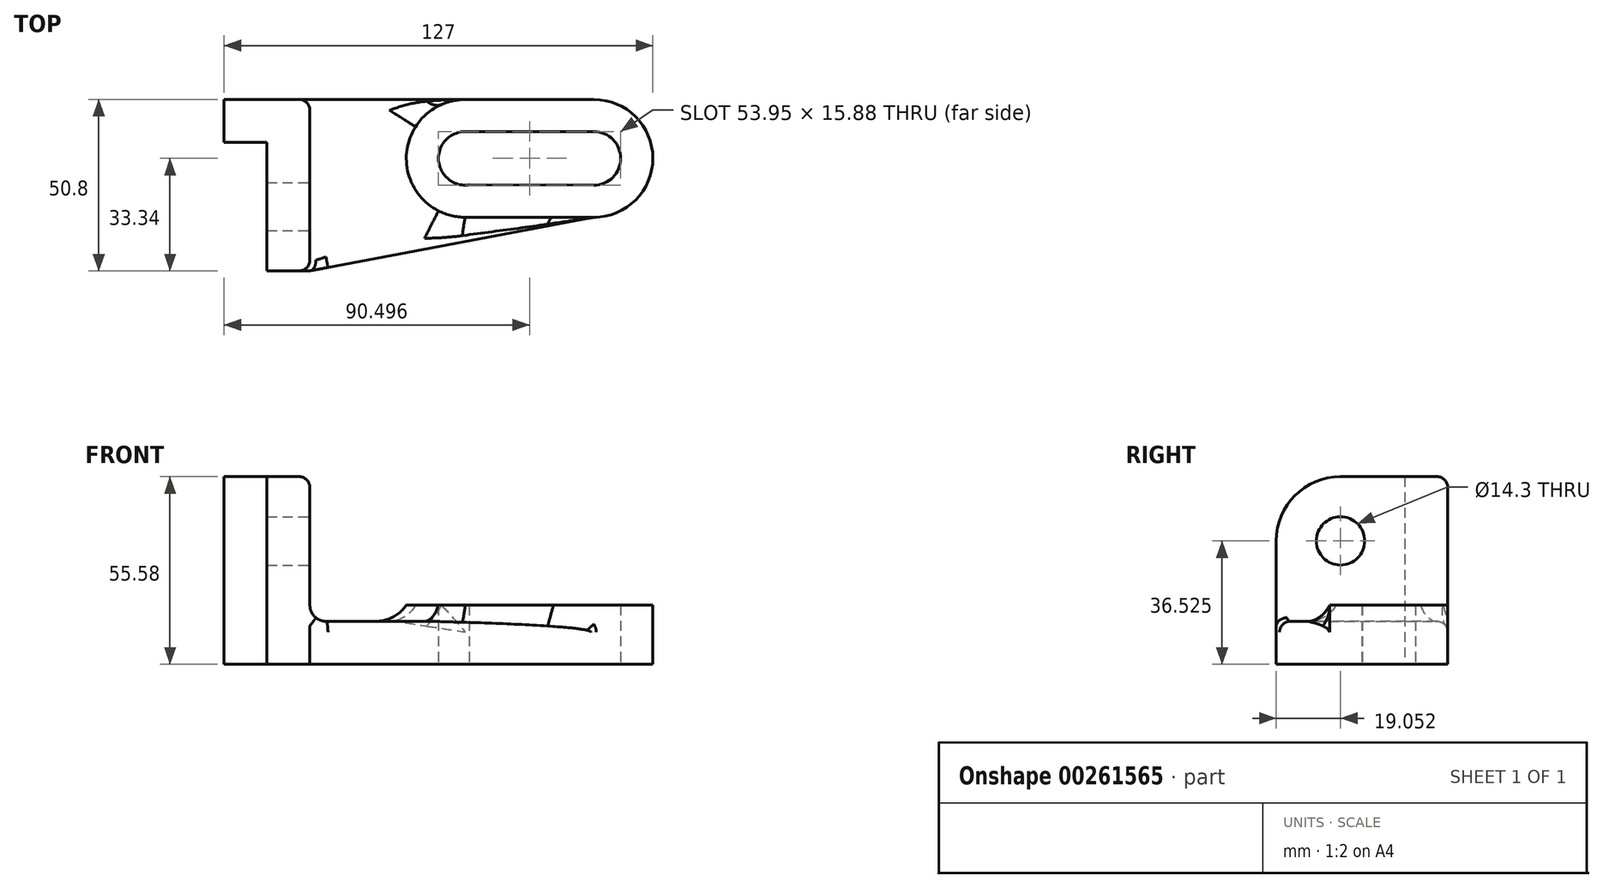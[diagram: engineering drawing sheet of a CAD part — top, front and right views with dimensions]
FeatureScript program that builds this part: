
annotation { "Feature Type Name" : "Feature", "Feature Type Description" : "" }
export const myFeature = defineFeature(function(context is Context, id is Id, definition is map)
    precondition{}
    {
        {
            var Q0;
            Q0=qCreatedBy(makeId("Top.planeOp"),FACE);
            var sketch = newSketch(context, id + "F0", { "sketchPlane" : qUnion([Q0])});
            skArc(sketch, "E0", {"start": v(-25.36, 8.79) * mm, "mid": v(-7.9, 26.25) * mm, "end": v(-25.36, 43.71) * mm});
            skArc(sketch, "E1", {"start": v(-25.36, 18.31) * mm, "mid": v(-17.43, 26.25) * mm, "end": v(-25.36, 34.19) * mm});
            skLineSegment(sketch, "E2", {"start": v(-25.36, 43.71) * mm, "end": v(-63.45, 43.71) * mm});
            skLineSegment(sketch, "E3", {"start": v(-25.36, 8.79) * mm, "end": v(-63.46, 8.79) * mm});
            skArc(sketch, "E4", {"start": v(-63.45, 43.71) * mm, "mid": v(-80.93, 26.26) * mm, "end": v(-63.46, 8.79) * mm});
            skArc(sketch, "E5", {"start": v(-63.46, 34.19) * mm, "mid": v(-71.38, 25.67) * mm, "end": v(-62.3, 18.4) * mm});
            skLineSegment(sketch, "E6", {"start": v(-63.46, 34.19) * mm, "end": v(-25.36, 34.19) * mm});
            skLineSegment(sketch, "E7", {"start": v(-64.66, 18.4) * mm, "end": v(-25.36, 18.31) * mm});
            skLineSegment(sketch, "E8", {"start": v(-63.45, 43.71) * mm, "end": v(-109.5, 43.71) * mm});
            skLineSegment(sketch, "E9", {"start": v(-109.5, 43.71) * mm, "end": v(-109.5, -7.09) * mm});
            skLineSegment(sketch, "E10", {"start": v(-109.5, -7.09) * mm, "end": v(-25.36, 8.79) * mm});
            skLineSegment(sketch, "E11", {"start": v(-109.5, 43.71) * mm, "end": v(-122.2, 43.71) * mm});
            skLineSegment(sketch, "E12", {"start": v(-122.2, 31.01) * mm, "end": v(-122.2, -7.09) * mm});
            skLineSegment(sketch, "E13", {"start": v(-122.2, -7.09) * mm, "end": v(-109.5, -7.09) * mm});
            skLineSegment(sketch, "E14", {"start": v(-122.2, 31.01) * mm, "end": v(-134.9, 31.01) * mm});
            skLineSegment(sketch, "E15", {"start": v(-134.9, 31.01) * mm, "end": v(-134.9, 43.71) * mm});
            skLineSegment(sketch, "E16", {"start": v(-134.9, 43.71) * mm, "end": v(-122.2, 43.71) * mm});
            skSolve(sketch);
        }
        {
            var Q0;
            Q0 = qSketchRegion(id + "F0", true);
            extrude(context, id + "F1", {"entities" : qUnion([Q0]), "depth" : 12.7 * mm});
        }
        {
            var Q0;
            Q0=makeQuery(id+"F0.imprint","IMPRINT",FACE,{"disambiguationData":[TD([[makeQuery(id+"F0.imprint","IMPRINT",EDGE,{"derivedFrom":sQuery(id+"F0.wireOp",EDGE,"E0")}),1.0]])]});
            extrude(context, id + "F2", {"entities" : qUnion([Q0]), "operationType" : NewBodyOperationType.ADD, "depth" : 17.48 * mm});
        }
        {
            var Q0;
            Q0=makeQuery(id+"F0.imprint","IMPRINT",FACE,{"disambiguationData":[TD([[makeQuery(id+"F0.imprint","IMPRINT",EDGE,{"derivedFrom":sQuery(id+"F0.wireOp",EDGE,"E9")}),-1.0]])]});
            extrude(context, id + "F3", {"entities" : qUnion([Q0]), "operationType" : NewBodyOperationType.ADD, "depth" : 55.58 * mm});
        }
        {
            var Q0;
            Q0=makeQuery(id+"F3.boolean.opBoolean","INTERSECT",EDGE,{"derivedFrom":[makeQuery(id+"F1.opExtrude","CAP_FACE",FACE,{"disambiguationData":[OSD([sQuery(id+"F0.wireOp",EDGE,"E0"),sQuery(id+"F0.wireOp",EDGE,"E1"),sQuery(id+"F0.wireOp",EDGE,"E2"),sQuery(id+"F0.wireOp",EDGE,"E5"),sQuery(id+"F0.wireOp",EDGE,"E6"),sQuery(id+"F0.wireOp",EDGE,"E7"),sQuery(id+"F0.wireOp",EDGE,"E8"),sQuery(id+"F0.wireOp",EDGE,"E10"),sQuery(id+"F0.wireOp",EDGE,"E11"),sQuery(id+"F0.wireOp",EDGE,"E12"),sQuery(id+"F0.wireOp",EDGE,"E13"),sQuery(id+"F0.wireOp",EDGE,"E14"),sQuery(id+"F0.wireOp",EDGE,"E15"),sQuery(id+"F0.wireOp",EDGE,"E16")])],"isStart":false}),makeQuery(id+"F3.opExtrude","SWEPT_FACE",FACE,{"disambiguationData":[OSD([sQuery(id+"F0.wireOp",EDGE,"E9")])]})]});
            fillet(context, id + "F4", {"entities" : qUnion([Q0]), "radius" : 4.78 * mm, "tangentPropagation" : true, "allowEdgeOverflow" : false});
        }
        {
            var Q0;
            Q0=makeQuery(id+"F3.opExtrude","SWEPT_FACE",FACE,{"disambiguationData":[OSD([sQuery(id+"F0.wireOp",EDGE,"E9")])]});
            var sketch = newSketch(context, id + "F5", { "sketchPlane" : qUnion([Q0])});
            skLineSegment(sketch, "E17", {"start": v(11.96, 55.58) * mm, "end": v(11.96, 36.53) * mm, "construction": true});
            skCircle(sketch, "E18", {"center": v(11.96, 36.53) * mm, "radius": 19.05 * mm});
            skCircle(sketch, "E19", {"center": v(11.96, 36.53) * mm, "radius": 7.15 * mm});
            skSolve(sketch);
        }
        {
            var Q0;
            {var subQ0=sQuery(id+"F5.wireOp",EDGE,"E18");var subQ1=sQuery(id+"F0.wireOp",EDGE,"E9");var subQ4=makeQuery(id+"F3.opExtrude","CAP_EDGE",EDGE,{"disambiguationData":[OSD([subQ1])],"isStart":false});var subQ5=makeQuery(id+"F5.imprint","INTERSECT",VERTEX,{"derivedFrom":[subQ4,subQ0]});Q0=makeQuery(id+"F5.imprint","IMPRINT",FACE,{"disambiguationData":[TD([[makeQuery(id+"F5.imprint","IMPRINT",EDGE,{"disambiguationData":[TD([[subQ5,-1.0]])],"derivedFrom":subQ0}),-1.0]])]});}
            extrude(context, id + "F6", {"entities" : qUnion([Q0]), "operationType" : NewBodyOperationType.REMOVE, "oppositeDirection" : true, "depth" : 25.4 * mm});
        }
        {
            var Q0;
            Q0=sQuery(id+"F5.wireOp",VERTEX,"E19.center");
            var Q1;
            Q1=makeQuery(id+"F1.opExtrude","SWEPT_BODY",BODY,{"disambiguationData":[OSD([sQuery(id+"F0.wireOp",EDGE,"E0"),sQuery(id+"F0.wireOp",EDGE,"E1"),sQuery(id+"F0.wireOp",EDGE,"E2"),sQuery(id+"F0.wireOp",EDGE,"E5"),sQuery(id+"F0.wireOp",EDGE,"E6"),sQuery(id+"F0.wireOp",EDGE,"E7"),sQuery(id+"F0.wireOp",EDGE,"E8"),sQuery(id+"F0.wireOp",EDGE,"E10"),sQuery(id+"F0.wireOp",EDGE,"E11"),sQuery(id+"F0.wireOp",EDGE,"E12"),sQuery(id+"F0.wireOp",EDGE,"E13"),sQuery(id+"F0.wireOp",EDGE,"E14"),sQuery(id+"F0.wireOp",EDGE,"E15"),sQuery(id+"F0.wireOp",EDGE,"E16")])]});
            hole(context, id + "F7", {"style" : HoleStyle.SIMPLE, "endStyle" : HoleEndStyle.THROUGH, "holeDiameter" : 14.3 * mm, "tappedDepth" : 12.7 * mm, "tapClearance" : 3, "locations" : qUnion([Q0]), "scope" : qUnion([Q1])});
        }
        {
            var Q0;
            Q0=makeQuery(id+"F6.boolean.opBoolean","COPY",EDGE,{"derivedFrom":makeQuery(id+"F6.opExtrude","CAP_EDGE",EDGE,{"disambiguationData":[OSD([sQuery(id+"F5.wireOp",EDGE,"E18")])],"isStart":true})});
            var Q1;
            Q1=makeQuery(id+"F3.opExtrude","CAP_EDGE",EDGE,{"disambiguationData":[OSD([sQuery(id+"F0.wireOp",EDGE,"E9")])],"isStart":false});
            var Q2;
            Q2=makeQuery(id+"F3.opExtrude","SWEPT_EDGE",EDGE,{"disambiguationData":[OSD([sQuery(id+"F0.wireOp",EDGE,"E9"),sQuery(id+"F0.wireOp",EDGE,"E10"),sQuery(id+"F0.wireOp",EDGE,"E13")])]});
            fillet(context, id + "F8", {"entities" : qUnion([Q0, Q1, Q2]), "radius" : 3.17 * mm, "tangentPropagation" : true, "allowEdgeOverflow" : false});
        }
        {
            var Q0;
            Q0=makeQuery(id+"F1.opExtrude","CAP_EDGE",EDGE,{"disambiguationData":[OSD([sQuery(id+"F0.wireOp",EDGE,"E10")])],"isStart":false});
            fillet(context, id + "F9", {"entities" : qUnion([Q0]), "radius" : 3.17 * mm, "tangentPropagation" : true, "allowEdgeOverflow" : false});
        }
        {
            var Q0;
            Q0=makeQuery(id+"F1.opExtrude","CAP_EDGE",EDGE,{"disambiguationData":[OSD([sQuery(id+"F0.wireOp",EDGE,"E2"),sQuery(id+"F0.wireOp",EDGE,"E8"),sQuery(id+"F0.wireOp",EDGE,"E11"),sQuery(id+"F0.wireOp",EDGE,"E16")])],"isStart":false});
            var Q1;
            Q1=makeQuery(id+"F3.opExtrude","SWEPT_EDGE",EDGE,{"disambiguationData":[OSD([sQuery(id+"F0.wireOp",EDGE,"E8"),sQuery(id+"F0.wireOp",EDGE,"E9"),sQuery(id+"F0.wireOp",EDGE,"E11")])]});
            fillet(context, id + "F10", {"entities" : qUnion([Q0, Q1]), "radius" : 3.17 * mm, "tangentPropagation" : true, "allowEdgeOverflow" : false});
        }
        {
            var Q0;
            Q0=makeQuery(id+"F2.boolean.opBoolean","INTERSECT",EDGE,{"derivedFrom":[makeQuery(id+"F1.opExtrude","CAP_FACE",FACE,{"disambiguationData":[OSD([sQuery(id+"F0.wireOp",EDGE,"E0"),sQuery(id+"F0.wireOp",EDGE,"E1"),sQuery(id+"F0.wireOp",EDGE,"E2"),sQuery(id+"F0.wireOp",EDGE,"E5"),sQuery(id+"F0.wireOp",EDGE,"E6"),sQuery(id+"F0.wireOp",EDGE,"E7"),sQuery(id+"F0.wireOp",EDGE,"E8"),sQuery(id+"F0.wireOp",EDGE,"E10"),sQuery(id+"F0.wireOp",EDGE,"E11"),sQuery(id+"F0.wireOp",EDGE,"E12"),sQuery(id+"F0.wireOp",EDGE,"E13"),sQuery(id+"F0.wireOp",EDGE,"E14"),sQuery(id+"F0.wireOp",EDGE,"E15"),sQuery(id+"F0.wireOp",EDGE,"E16")])],"isStart":false}),makeQuery(id+"F2.opExtrude","SWEPT_FACE",FACE,{"disambiguationData":[OSD([sQuery(id+"F0.wireOp",EDGE,"E4")])]})]});
            var Q1;
            Q1=makeQuery(id+"F2.boolean.opBoolean","INTERSECT",EDGE,{"derivedFrom":[makeQuery(id+"F1.opExtrude","CAP_FACE",FACE,{"disambiguationData":[OSD([sQuery(id+"F0.wireOp",EDGE,"E0"),sQuery(id+"F0.wireOp",EDGE,"E1"),sQuery(id+"F0.wireOp",EDGE,"E2"),sQuery(id+"F0.wireOp",EDGE,"E5"),sQuery(id+"F0.wireOp",EDGE,"E6"),sQuery(id+"F0.wireOp",EDGE,"E7"),sQuery(id+"F0.wireOp",EDGE,"E8"),sQuery(id+"F0.wireOp",EDGE,"E10"),sQuery(id+"F0.wireOp",EDGE,"E11"),sQuery(id+"F0.wireOp",EDGE,"E12"),sQuery(id+"F0.wireOp",EDGE,"E13"),sQuery(id+"F0.wireOp",EDGE,"E14"),sQuery(id+"F0.wireOp",EDGE,"E15"),sQuery(id+"F0.wireOp",EDGE,"E16")])],"isStart":false}),makeQuery(id+"F2.opExtrude","SWEPT_FACE",FACE,{"disambiguationData":[OSD([sQuery(id+"F0.wireOp",EDGE,"E3")])]})]});
            fillet(context, id + "F11", {"entities" : qUnion([Q0, Q1]), "radius" : 11.13 * mm, "tangentPropagation" : true, "allowEdgeOverflow" : false});
        }
    });
